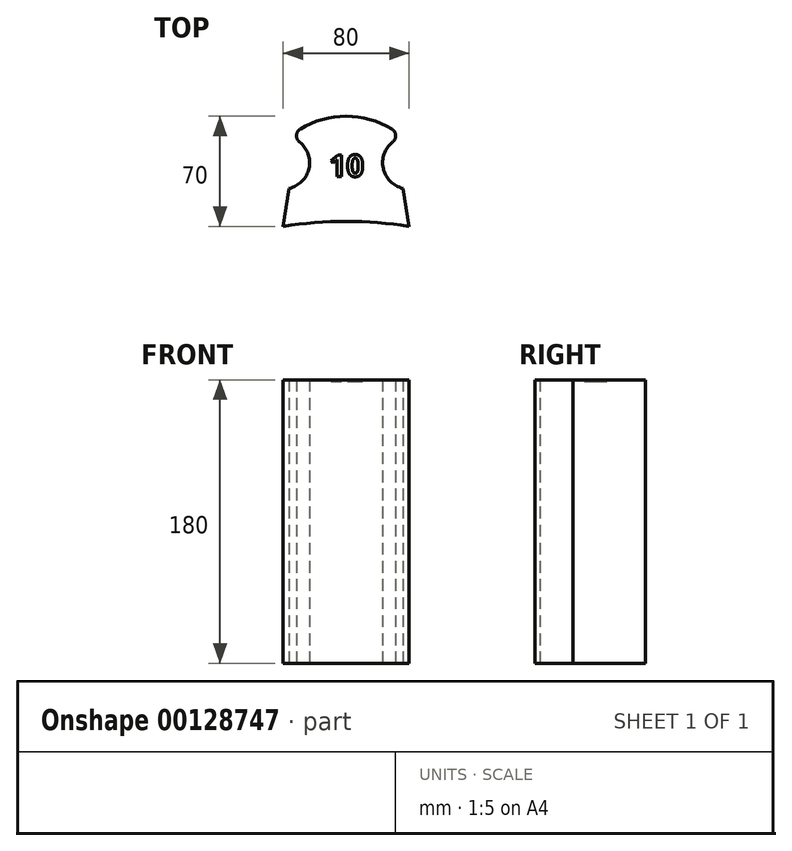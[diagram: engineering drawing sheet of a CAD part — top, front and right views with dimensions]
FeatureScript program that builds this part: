
annotation { "Feature Type Name" : "Feature", "Feature Type Description" : "" }
export const myFeature = defineFeature(function(context is Context, id is Id, definition is map)
    precondition{}
    {
        {
            var Q0;
            Q0=qCreatedBy(makeId("Top.planeOp"),FACE);
            var sketch = newSketch(context, id + "F0", { "sketchPlane" : qUnion([Q0])});
            skLineSegment(sketch, "E0", {"start": v(0, 0) * mm, "end": v(3.87, 24.16) * mm});
            skLineSegment(sketch, "E1", {"start": v(0, 0) * mm, "end": v(80, 0) * mm, "construction": true});
            skLineSegment(sketch, "E2", {"start": v(40, 0) * mm, "end": v(40, 70) * mm, "construction": true});
            skArc(sketch, "E3", {"start": v(3.87, 24.16) * mm, "mid": v(16.4, 36.85) * mm, "end": v(10.4, 53.64) * mm});
            skArc(sketch, "E4.MirrorCS", {"start": v(76.13, 24.16) * mm, "mid": v(63.6, 36.85) * mm, "end": v(69.6, 53.64) * mm});
            skLineSegment(sketch, "E5.MirrorCS", {"start": v(80, 0) * mm, "end": v(76.13, 24.16) * mm});
            skArc(sketch, "E6", {"start": v(69.1, 61.84) * mm, "mid": v(40, 70) * mm, "end": v(10.9, 61.84) * mm});
            skPoint(sketch, "E7.visualSharp", {"position": v(3.87, 56.79) * mm});
            skArc(sketch, "E7.filletArc", {"start": v(10.9, 61.84) * mm, "mid": v(8.5, 57.87) * mm, "end": v(10.4, 53.64) * mm});
            skPoint(sketch, "E8.visualSharp", {"position": v(76.13, 56.79) * mm});
            skArc(sketch, "E8.filletArc", {"start": v(69.6, 53.64) * mm, "mid": v(71.5, 57.87) * mm, "end": v(69.1, 61.84) * mm});
            skArc(sketch, "E9.MirrorCS", {"start": v(0, 0) * mm, "mid": v(40, 3.18) * mm, "end": v(80, 0) * mm});
            skSolve(sketch);
        }
        {
            var Q0;
            Q0=makeQuery(id+"F0.imprint","IMPRINT",FACE,{"disambiguationData":[TD([[makeQuery(id+"F0.imprint","IMPRINT",EDGE,{"derivedFrom":sQuery(id+"F0.wireOp",EDGE,"E0")}),-1.0]])]});
            extrude(context, id + "F1", {"entities" : qUnion([Q0]), "depth" : 180 * mm});
        }
        {
            var Q0;
            Q0=makeQuery(id+"F1.opExtrude","CAP_FACE",FACE,{"disambiguationData":[OSD([sQuery(id+"F0.wireOp",EDGE,"E0"),sQuery(id+"F0.wireOp",EDGE,"E3"),sQuery(id+"F0.wireOp",EDGE,"E4.MirrorCS"),sQuery(id+"F0.wireOp",EDGE,"E5.MirrorCS"),sQuery(id+"F0.wireOp",EDGE,"E6"),sQuery(id+"F0.wireOp",EDGE,"E7.filletArc"),sQuery(id+"F0.wireOp",EDGE,"E8.filletArc"),sQuery(id+"F0.wireOp",EDGE,"NzHJaS1e-Hx9R-e02U-jfAq-aO6yktXq1YBm")])],"isStart":false});
            var sketch = newSketch(context, id + "F2", { "sketchPlane" : qUnion([Q0])});
            skText(sketch, "E10", { "text": "10", "fontName": "OpenSans-Bold.ttf"});
            skPoint(sketch, "E11", {"position": v(40, 70) * mm});
            const initialGuessF2  = {"E10": [0.02922, 0.03166, 1, 0, 0.0139]};
            skSetInitialGuess(sketch, initialGuessF2);
            skSolve(sketch);
        }
        {
            var Q0;
            Q0=qSketchRegion(id+"F2",true);
            extrude(context, id + "F3", {"entities" : qUnion([Q0]), "operationType" : NewBodyOperationType.REMOVE, "oppositeDirection" : true, "depth" : 1 * mm});
        }
    });
